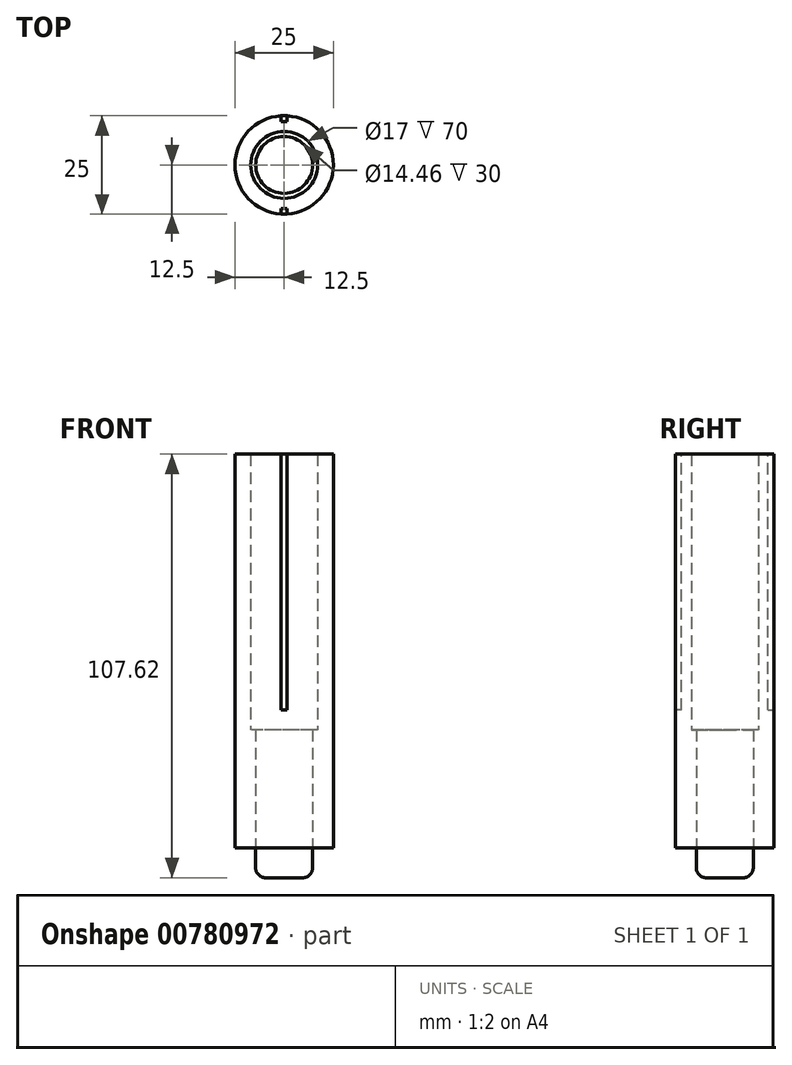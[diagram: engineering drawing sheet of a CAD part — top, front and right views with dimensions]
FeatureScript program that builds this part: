
annotation { "Feature Type Name" : "Feature", "Feature Type Description" : "" }
export const myFeature = defineFeature(function(context is Context, id is Id, definition is map)
    precondition{}
    {
        {
            var Q0;
            Q0=qCreatedBy(makeId("Top.planeOp"),FACE);
            var sketch = newSketch(context, id + "F0", { "sketchPlane" : qUnion([Q0])});
            skCircle(sketch, "E0", {"center": v(0, 0) * mm, "radius": 8.5 * mm});
            skCircle(sketch, "E1.0", {"center": v(0, 0) * mm, "radius": 12.5 * mm});
            skCircle(sketch, "E2.0", {"center": v(0, 0) * mm, "radius": 7.23 * mm});
            skSolve(sketch);
        }
        {
            var Q0;
            Q0=makeQuery(id+"F0.imprint","IMPRINT",FACE,{"disambiguationData":[TD([[makeQuery(id+"F0.imprint","IMPRINT",EDGE,{"derivedFrom":sQuery(id+"F0.wireOp",EDGE,"E0")}),-1.0]])]});
            var Q1;
            Q1 = qSketchRegion(id + "F4", true);
            extrude(context, id + "F1", {"entities" : qUnion([Q0, Q1]), "depth" : 100 * mm, "offsetDistance" : 25.4 * mm});
        }
        {
            var Q0;
            Q0=makeQuery(id+"F0.imprint","IMPRINT",FACE,{"disambiguationData":[TD([[makeQuery(id+"F0.imprint","IMPRINT",EDGE,{"derivedFrom":sQuery(id+"F0.wireOp",EDGE,"E0")}),1.0]])]});
            extrude(context, id + "F2", {"entities" : qUnion([Q0]), "operationType" : NewBodyOperationType.ADD, "depth" : 5.08 * mm, "offsetDistance" : 25.4 * mm});
        }
        {
            var Q0;
            Q0=makeQuery(id+"F0.imprint","IMPRINT",FACE,{"disambiguationData":[TD([[makeQuery(id+"F0.imprint","IMPRINT",EDGE,{"derivedFrom":sQuery(id+"F0.wireOp",EDGE,"E0")}),1.0]])]});
            extrude(context, id + "F3", {"entities" : qUnion([Q0]), "operationType" : NewBodyOperationType.ADD, "depth" : 30 * mm, "offsetDistance" : 25.4 * mm});
        }
        {
            var Q0;
            Q0=qCreatedBy(makeId("Top.planeOp"),FACE);
            var sketch = newSketch(context, id + "F4", { "sketchPlane" : qUnion([Q0])});
            skSolve(sketch);
        }
        {
            var Q0;
            Q0=makeQuery(id+"F0.imprint","IMPRINT",FACE,{"disambiguationData":[TD([[makeQuery(id+"F0.imprint","IMPRINT",EDGE,{"derivedFrom":sQuery(id+"F0.wireOp",EDGE,"E2.0")}),1.0]])]});
            extrude(context, id + "F5", {"entities" : qUnion([Q0]), "depth" : -7.62 * mm, "offsetDistance" : 25.4 * mm});
        }
        {
            var Q0;
            Q0=makeQuery(id+"F5.opExtrude","CAP_EDGE",EDGE,{"disambiguationData":[OSD([sQuery(id+"F0.wireOp",EDGE,"E2.0")])],"isStart":false});
            fillet(context, id + "F6", {"entities" : qUnion([Q0]), "radius" : 2.54 * mm, "tangentPropagation" : true, "allowEdgeOverflow" : false});
        }
        {
            var Q0;
            Q0=makeQuery(id+"F1.opExtrude","CAP_FACE",FACE,{"disambiguationData":[OSD([sQuery(id+"F0.wireOp",EDGE,"E0"),sQuery(id+"F0.wireOp",EDGE,"E1.0")])],"isStart":false});
            var sketch = newSketch(context, id + "F7", { "sketchPlane" : qUnion([Q0])});
            skLineSegment(sketch, "E3", {"start": v(0, 11.04) * mm, "end": v(-0.79, 11.04) * mm});
            skLineSegment(sketch, "E4", {"start": v(-0.79, 11.04) * mm, "end": v(-0.79, 16.8) * mm});
            skLineSegment(sketch, "E5", {"start": v(-0.79, 16.8) * mm, "end": v(0, 16.8) * mm});
            skLineSegment(sketch, "E6.MirrorCS", {"start": v(0.79, 11.04) * mm, "end": v(0.79, 16.8) * mm});
            skLineSegment(sketch, "E7.MirrorCS", {"start": v(0, 11.04) * mm, "end": v(0.79, 11.04) * mm});
            skLineSegment(sketch, "E8.MirrorCS", {"start": v(0.79, 16.8) * mm, "end": v(0, 16.8) * mm});
            skLineSegment(sketch, "E9.MirrorCS", {"start": v(-0.79, -11.04) * mm, "end": v(-0.79, -16.8) * mm});
            skLineSegment(sketch, "E10.MirrorCS", {"start": v(0.79, -11.04) * mm, "end": v(0.79, -16.8) * mm});
            skLineSegment(sketch, "E11.MirrorCS", {"start": v(0, -11.04) * mm, "end": v(0.79, -11.04) * mm});
            skLineSegment(sketch, "E12.MirrorCS", {"start": v(0, -11.04) * mm, "end": v(-0.79, -11.04) * mm});
            skLineSegment(sketch, "E13.MirrorCS", {"start": v(-0.79, -16.8) * mm, "end": v(0, -16.8) * mm});
            skLineSegment(sketch, "E14.MirrorCS", {"start": v(0.79, -16.8) * mm, "end": v(0, -16.8) * mm});
            skSolve(sketch);
        }
        {
            var Q0;
            Q0 = qSketchRegion(id + "F7", true);
            extrude(context, id + "F8", {"entities" : qUnion([Q0]), "operationType" : NewBodyOperationType.REMOVE, "oppositeDirection" : true, "depth" : 65 * mm, "offsetDistance" : 25.4 * mm});
        }
    });
